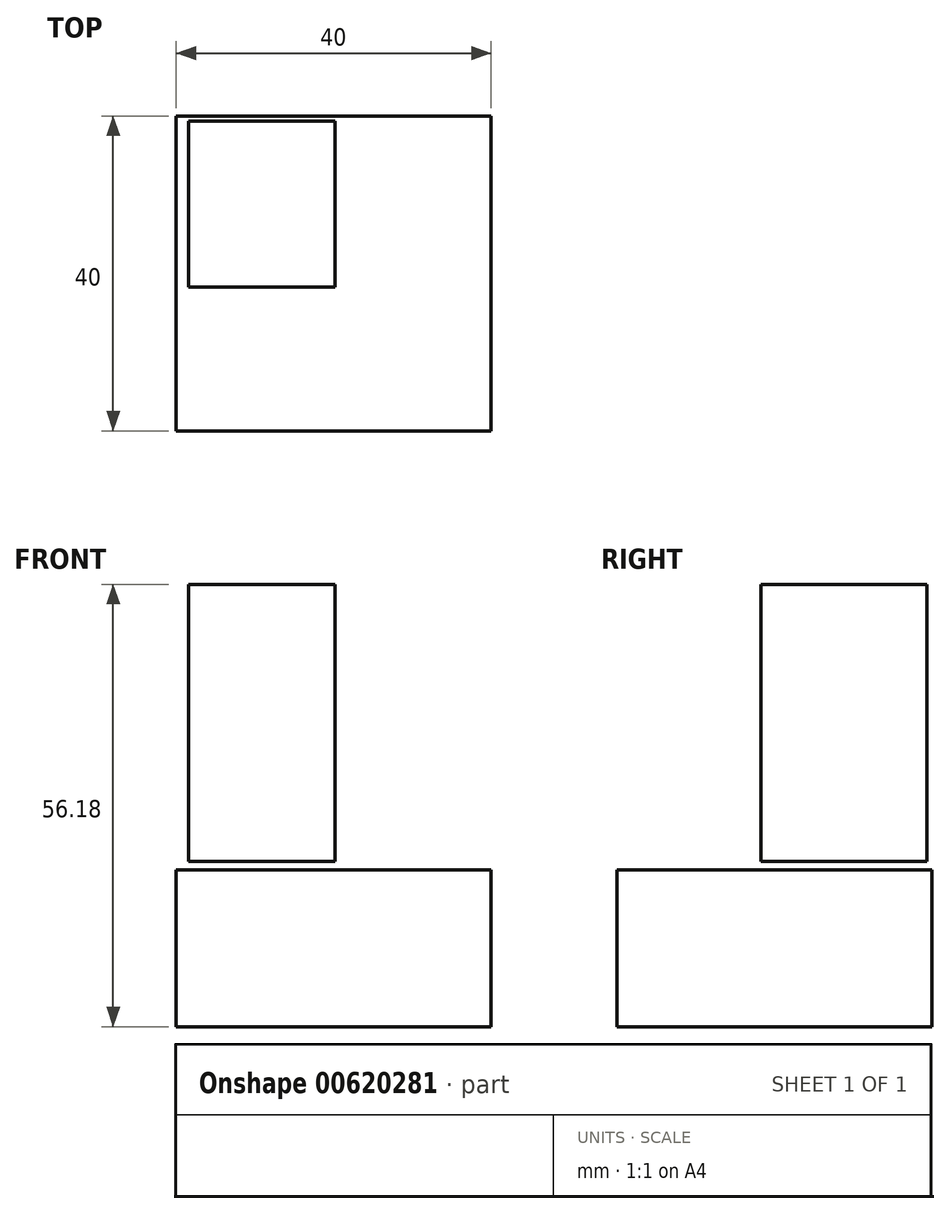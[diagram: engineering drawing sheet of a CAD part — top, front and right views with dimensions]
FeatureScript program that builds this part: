
annotation { "Feature Type Name" : "Feature", "Feature Type Description" : "" }
export const myFeature = defineFeature(function(context is Context, id is Id, definition is map)
    precondition{}
    {
        {
            var Q0;
            Q0=qCreatedBy(makeId("Top.planeOp"),FACE);
            var sketch = newSketch(context, id + "F0", { "sketchPlane" : qUnion([Q0])});
            skLineSegment(sketch, "E0.bottom", {"start": v(-32.8, 21.73) * mm, "end": v(7.2, 21.73) * mm});
            skLineSegment(sketch, "E0.top", {"start": v(-32.8, -18.27) * mm, "end": v(7.2, -18.27) * mm});
            skLineSegment(sketch, "E0.left", {"start": v(-32.8, 21.73) * mm, "end": v(-32.8, -18.27) * mm});
            skLineSegment(sketch, "E0.right", {"start": v(7.2, 21.73) * mm, "end": v(7.2, -18.27) * mm});
            skSolve(sketch);
        }
        {
            var Q0;
            Q0 = qSketchRegion(id + "F0", true);
            extrude(context, id + "F1", {"entities" : qUnion([Q0]), "depth" : 19.9 * mm, "offsetDistance" : 25 * mm});
        }
        {
            var Q0;
            Q0=qCreatedBy(makeId("Front.planeOp"),FACE);
            var sketch = newSketch(context, id + "F2", { "sketchPlane" : qUnion([Q0])});
            skLineSegment(sketch, "E1.bottom", {"start": v(-31.23, 20.98) * mm, "end": v(-12.61, 20.98) * mm});
            skLineSegment(sketch, "E1.top", {"start": v(-31.23, 56.18) * mm, "end": v(-12.61, 56.18) * mm});
            skLineSegment(sketch, "E1.left", {"start": v(-31.23, 20.98) * mm, "end": v(-31.23, 56.18) * mm});
            skLineSegment(sketch, "E1.right", {"start": v(-12.61, 20.98) * mm, "end": v(-12.61, 56.18) * mm});
            skSolve(sketch);
        }
        {
            var Q0;
            Q0 = qSketchRegion(id + "F2", true);
            extrude(context, id + "F3", {"entities" : qUnion([Q0]), "oppositeDirection" : true, "depth" : 21.1 * mm, "offsetDistance" : 25 * mm});
        }
    });
